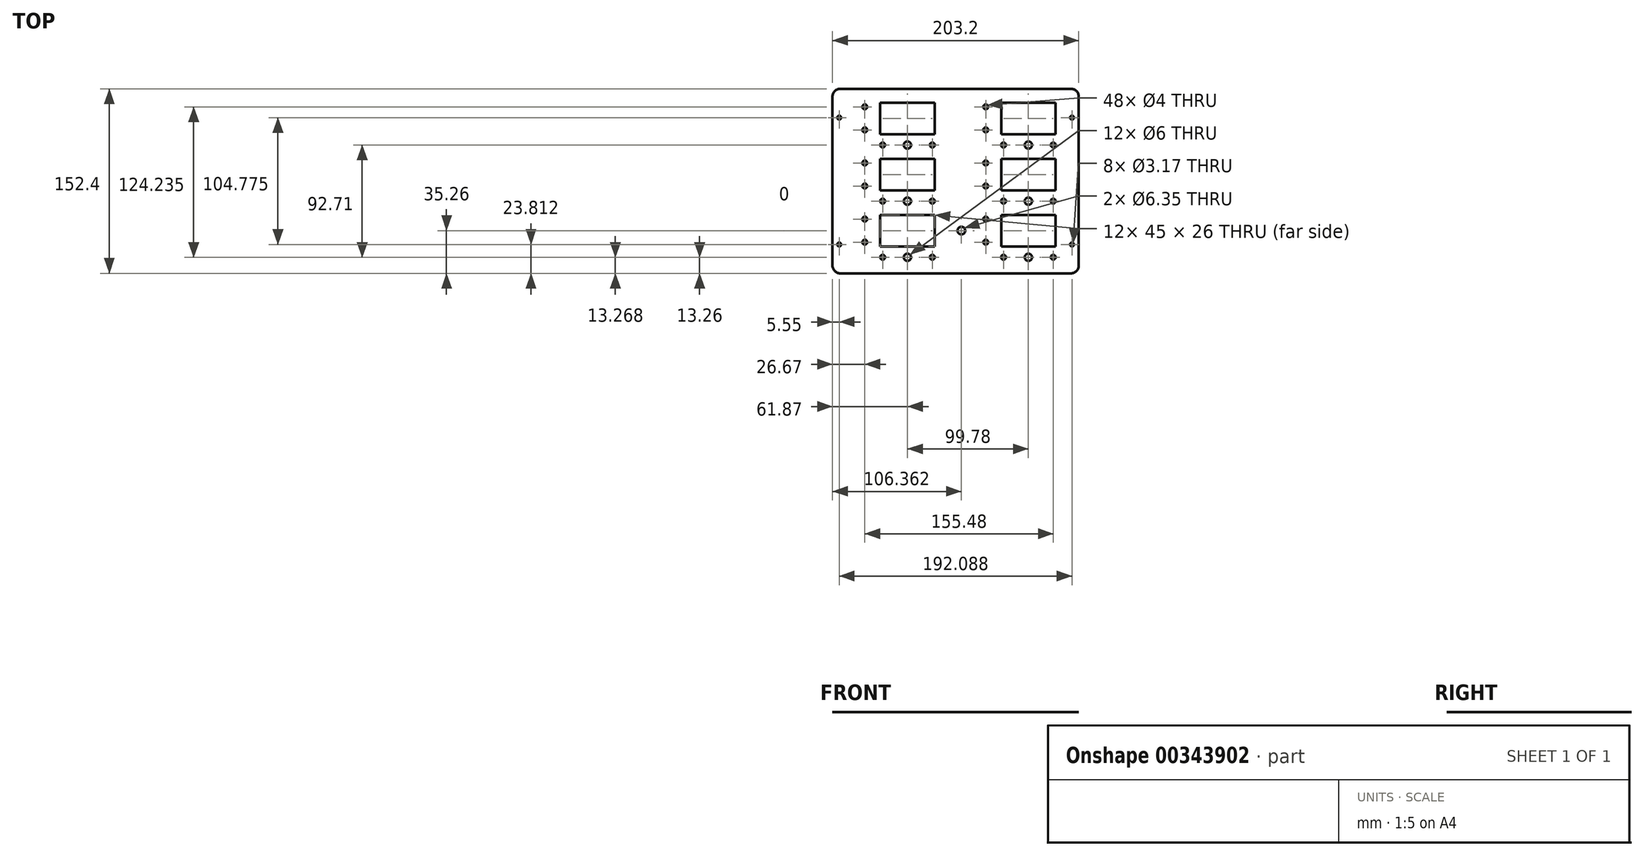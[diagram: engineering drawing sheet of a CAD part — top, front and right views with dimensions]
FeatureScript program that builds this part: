
annotation { "Feature Type Name" : "Feature", "Feature Type Description" : "" }
export const myFeature = defineFeature(function(context is Context, id is Id, definition is map)
    precondition{}
    {
        {
            var Q0;
            Q0=qCreatedBy(makeId("Top.planeOp"),FACE);
            var sketch = newSketch(context, id + "F0", { "sketchPlane" : qUnion([Q0])});
            skLineSegment(sketch, "E0.bottom", {"start": v(6.35, 0) * mm, "end": v(196.85, 0) * mm});
            skLineSegment(sketch, "E0.top", {"start": v(6.35, 152.4) * mm, "end": v(196.85, 152.4) * mm});
            skLineSegment(sketch, "E0.left", {"start": v(0, 6.35) * mm, "end": v(0, 146.05) * mm});
            skLineSegment(sketch, "E0.right", {"start": v(203.2, 6.35) * mm, "end": v(203.2, 146.05) * mm});
            skPoint(sketch, "E1.visualSharp", {"position": v(0, 0) * mm});
            skArc(sketch, "E1.filletArc", {"start": v(0, 6.35) * mm, "mid": v(1.86, 1.86) * mm, "end": v(6.35, 0) * mm});
            skPoint(sketch, "E2.visualSharp", {"position": v(203.2, 0) * mm});
            skArc(sketch, "E2.filletArc", {"start": v(196.85, 0) * mm, "mid": v(201.34, 1.86) * mm, "end": v(203.2, 6.35) * mm});
            skPoint(sketch, "E3.visualSharp", {"position": v(203.2, 152.4) * mm});
            skArc(sketch, "E3.filletArc", {"start": v(203.2, 146.05) * mm, "mid": v(201.34, 150.54) * mm, "end": v(196.85, 152.4) * mm});
            skPoint(sketch, "E4.visualSharp", {"position": v(0, 152.4) * mm});
            skArc(sketch, "E4.filletArc", {"start": v(6.35, 152.4) * mm, "mid": v(1.86, 150.54) * mm, "end": v(0, 146.05) * mm});
            skSolve(sketch);
        }
        {
            assignVariable(context, id + "F1", {"name" : "PanelTopLayer", "anyValue" : 1 / 1625.6 * mm});
        }
        {
            assignVariable(context, id + "F2", {"name" : "PanelDepth", "anyValue" : 3 / 812.8 * mm});
        }
        {
            var Q0;
            Q0=makeQuery(id+"F0.imprint","IMPRINT",FACE,{"disambiguationData":[TD([[makeQuery(id+"F0.imprint","IMPRINT",EDGE,{"derivedFrom":sQuery(id+"F0.wireOp",EDGE,"E0.bottom")}),1.0]])]});
            extrude(context, id + "F3", {"entities" : qUnion([Q0]), "oppositeDirection" : true, "depth" : getVariable(context, 'PanelTopLayer')});
        }
        {
            var Q0;
            Q0=makeQuery(id+"F3.opExtrude","CAP_FACE",FACE,{"disambiguationData":[OSD([sQuery(id+"F0.wireOp",EDGE,"E0.bottom"),sQuery(id+"F0.wireOp",EDGE,"E0.top"),sQuery(id+"F0.wireOp",EDGE,"E0.left"),sQuery(id+"F0.wireOp",EDGE,"E0.right"),sQuery(id+"F0.wireOp",EDGE,"4eb8843b-68a4-456e-adec-9ead3661f281.filletArc"),sQuery(id+"F0.wireOp",EDGE,"3b2eceeb-73e7-411c-82d1-259add97614e.filletArc"),sQuery(id+"F0.wireOp",EDGE,"241cabb4-3010-4474-995e-d7eb64fd05fc.filletArc"),sQuery(id+"F0.wireOp",EDGE,"ce37bbed-e9fa-4a66-9d02-96ea8e3f6179.filletArc")])],"isStart":false});
            var sketch = newSketch(context, id + "F4", { "sketchPlane" : qUnion([Q0])});
            skLineSegment(sketch, "E5.bottom", {"start": v(196.85, -152.4) * mm, "end": v(6.35, -152.4) * mm});
            skLineSegment(sketch, "E5.top", {"start": v(196.85, 0) * mm, "end": v(6.35, 0) * mm});
            skLineSegment(sketch, "E5.left", {"start": v(203.2, -146.05) * mm, "end": v(203.2, -6.35) * mm});
            skLineSegment(sketch, "E5.right", {"start": v(0, -146.05) * mm, "end": v(0, -6.35) * mm});
            skPoint(sketch, "E6.visualSharp", {"position": v(203.2, -152.4) * mm});
            skArc(sketch, "E6.filletArc", {"start": v(196.85, -152.4) * mm, "mid": v(201.34, -150.54) * mm, "end": v(203.2, -146.05) * mm});
            skPoint(sketch, "E7.visualSharp", {"position": v(0, -152.4) * mm});
            skArc(sketch, "E7.filletArc", {"start": v(0, -146.05) * mm, "mid": v(1.86, -150.54) * mm, "end": v(6.35, -152.4) * mm});
            skPoint(sketch, "E8.visualSharp", {"position": v(0, 0) * mm});
            skArc(sketch, "E8.filletArc", {"start": v(6.35, 0) * mm, "mid": v(1.86, -1.86) * mm, "end": v(0, -6.35) * mm});
            skPoint(sketch, "E9.visualSharp", {"position": v(203.2, 0) * mm});
            skArc(sketch, "E9.filletArc", {"start": v(203.2, -6.35) * mm, "mid": v(201.34, -1.86) * mm, "end": v(196.85, 0) * mm});
            skSolve(sketch);
        }
        {
            var Q0;
            Q0=makeQuery(id+"F4.imprint","IMPRINT",FACE,{"disambiguationData":[TD([[makeQuery(id+"F4.imprint","IMPRINT",EDGE,{"derivedFrom":sQuery(id+"F4.wireOp",EDGE,"E5.bottom")}),1.0]])]});
            extrude(context, id + "F5", {"entities" : qUnion([Q0]), "depth" : getVariable(context, 'PanelDepth') - getVariable(context, 'PanelTopLayer')});
        }
        {
            var Q0;
            Q0=makeQuery(id+"F0.imprint","IMPRINT",FACE,{"disambiguationData":[TD([[makeQuery(id+"F0.imprint","IMPRINT",EDGE,{"derivedFrom":sQuery(id+"F0.wireOp",EDGE,"E0.bottom")}),1.0]])]});
            var sketch = newSketch(context, id + "F6", { "sketchPlane" : qUnion([Q0])});
            skLineSegment(sketch, "E10.bottom", {"start": v(139.15, 140.97) * mm, "end": v(184.15, 140.97) * mm});
            skLineSegment(sketch, "E10.top", {"start": v(139.15, 114.97) * mm, "end": v(184.15, 114.97) * mm});
            skLineSegment(sketch, "E10.left", {"start": v(139.15, 140.97) * mm, "end": v(139.15, 114.97) * mm});
            skLineSegment(sketch, "E10.right", {"start": v(184.15, 140.97) * mm, "end": v(184.15, 114.97) * mm});
            skLineSegment(sketch, "E11.0.1.0", {"start": v(139.15, 94.62) * mm, "end": v(184.15, 94.62) * mm});
            skLineSegment(sketch, "E11.0.1.1", {"start": v(139.15, 94.62) * mm, "end": v(139.15, 68.62) * mm});
            skLineSegment(sketch, "E11.0.1.2", {"start": v(139.15, 68.62) * mm, "end": v(184.15, 68.62) * mm});
            skLineSegment(sketch, "E11.0.1.3", {"start": v(184.15, 94.62) * mm, "end": v(184.15, 68.62) * mm});
            skLineSegment(sketch, "E11.0.2.0", {"start": v(139.15, 48.26) * mm, "end": v(184.15, 48.26) * mm});
            skLineSegment(sketch, "E11.0.2.1", {"start": v(139.15, 48.26) * mm, "end": v(139.15, 22.26) * mm});
            skLineSegment(sketch, "E11.0.2.2", {"start": v(139.15, 22.26) * mm, "end": v(184.15, 22.26) * mm});
            skLineSegment(sketch, "E11.0.2.3", {"start": v(184.15, 48.26) * mm, "end": v(184.15, 22.26) * mm});
            skLineSegment(sketch, "E11.1.0.0", {"start": v(39.37, 140.97) * mm, "end": v(84.37, 140.97) * mm});
            skLineSegment(sketch, "E11.1.0.1", {"start": v(39.37, 140.97) * mm, "end": v(39.37, 114.97) * mm});
            skLineSegment(sketch, "E11.1.0.2", {"start": v(39.37, 114.97) * mm, "end": v(84.37, 114.97) * mm});
            skLineSegment(sketch, "E11.1.0.3", {"start": v(84.37, 140.97) * mm, "end": v(84.37, 114.97) * mm});
            skLineSegment(sketch, "E11.1.1.0", {"start": v(39.37, 94.62) * mm, "end": v(84.37, 94.62) * mm});
            skLineSegment(sketch, "E11.1.1.1", {"start": v(39.37, 94.62) * mm, "end": v(39.37, 68.62) * mm});
            skLineSegment(sketch, "E11.1.1.2", {"start": v(39.37, 68.62) * mm, "end": v(84.37, 68.62) * mm});
            skLineSegment(sketch, "E11.1.1.3", {"start": v(84.37, 94.62) * mm, "end": v(84.37, 68.62) * mm});
            skLineSegment(sketch, "E11.1.2.0", {"start": v(39.37, 48.26) * mm, "end": v(84.37, 48.26) * mm});
            skLineSegment(sketch, "E11.1.2.1", {"start": v(39.37, 48.26) * mm, "end": v(39.37, 22.26) * mm});
            skLineSegment(sketch, "E11.1.2.2", {"start": v(39.37, 22.26) * mm, "end": v(84.37, 22.26) * mm});
            skLineSegment(sketch, "E11.1.2.3", {"start": v(84.37, 48.26) * mm, "end": v(84.37, 22.26) * mm});
            skLineSegment(sketch, "E11.direction1", {"start": v(139.15, 114.97) * mm, "end": v(39.37, 114.97) * mm, "construction": true});
            skLineSegment(sketch, "E11.direction2", {"start": v(139.15, 114.97) * mm, "end": v(139.15, 68.62) * mm, "construction": true});
            skSolve(sketch);
        }
        {
            var Q0;
            Q0=qSketchRegion(id+"F6",true);
            extrude(context, id + "F7", {"entities" : qUnion([Q0]), "operationType" : NewBodyOperationType.REMOVE, "oppositeDirection" : true, "depth" : (getVariable(context, 'PanelDepth'))});
        }
        {
            var Q0;
            Q0=makeQuery(id+"F0.imprint","IMPRINT",FACE,{"disambiguationData":[TD([[makeQuery(id+"F0.imprint","IMPRINT",EDGE,{"derivedFrom":sQuery(id+"F0.wireOp",EDGE,"E0.bottom")}),1.0]])]});
            var sketch = newSketch(context, id + "F8", { "sketchPlane" : qUnion([Q0])});
            skCircle(sketch, "E12", {"center": v(106.36, 35.26) * mm, "radius": 3.18 * mm});
            skCircle(sketch, "E13", {"center": v(126.45, 137.5) * mm, "radius": 2 * mm});
            skLineSegment(sketch, "E14.direction1", {"start": v(105.19, 137.5) * mm, "end": v(126.45, 137.5) * mm, "construction": true});
            skLineSegment(sketch, "E14.direction2", {"start": v(126.45, 137.5) * mm, "end": v(126.45, 118.44) * mm, "construction": true});
            skCircle(sketch, "E15", {"center": v(141.15, 105.97) * mm, "radius": 2 * mm});
            skCircle(sketch, "E16.1.0.0", {"center": v(182.15, 105.97) * mm, "radius": 2 * mm});
            skLineSegment(sketch, "E16.direction1", {"start": v(141.15, 105.97) * mm, "end": v(182.15, 105.97) * mm, "construction": true});
            skCircle(sketch, "E17.0.0.1", {"center": v(126.45, 118.44) * mm, "radius": 2 * mm});
            skCircle(sketch, "E18.0.1.0", {"center": v(182.15, 59.62) * mm, "radius": 2 * mm});
            skCircle(sketch, "E18.0.1.1", {"center": v(141.15, 59.62) * mm, "radius": 2 * mm});
            skLineSegment(sketch, "E18.0.1.2", {"start": v(141.15, 59.62) * mm, "end": v(182.15, 59.62) * mm, "construction": true});
            skCircle(sketch, "E18.0.1.3", {"center": v(126.45, 91.14) * mm, "radius": 2 * mm});
            skCircle(sketch, "E18.0.1.4", {"center": v(126.45, 72.09) * mm, "radius": 2 * mm});
            skLineSegment(sketch, "E18.0.1.5", {"start": v(126.45, 91.14) * mm, "end": v(126.45, 72.1) * mm, "construction": true});
            skLineSegment(sketch, "E18.0.1.6", {"start": v(105.19, 91.14) * mm, "end": v(126.45, 91.14) * mm, "construction": true});
            skCircle(sketch, "E18.0.2.0", {"center": v(182.15, 13.26) * mm, "radius": 2 * mm});
            skCircle(sketch, "E18.0.2.1", {"center": v(141.15, 13.26) * mm, "radius": 2 * mm});
            skLineSegment(sketch, "E18.0.2.2", {"start": v(141.15, 13.26) * mm, "end": v(182.15, 13.26) * mm, "construction": true});
            skCircle(sketch, "E18.0.2.3", {"center": v(126.45, 44.79) * mm, "radius": 2 * mm});
            skCircle(sketch, "E18.0.2.4", {"center": v(126.45, 25.73) * mm, "radius": 2 * mm});
            skLineSegment(sketch, "E18.0.2.5", {"start": v(126.45, 44.79) * mm, "end": v(126.45, 25.73) * mm, "construction": true});
            skLineSegment(sketch, "E18.0.2.6", {"start": v(105.19, 44.79) * mm, "end": v(126.45, 44.79) * mm, "construction": true});
            skCircle(sketch, "E18.1.0.0", {"center": v(82.37, 105.97) * mm, "radius": 2 * mm});
            skCircle(sketch, "E18.1.0.1", {"center": v(41.37, 105.97) * mm, "radius": 2 * mm});
            skLineSegment(sketch, "E18.1.0.2", {"start": v(41.37, 105.97) * mm, "end": v(82.37, 105.97) * mm, "construction": true});
            skCircle(sketch, "E18.1.0.3", {"center": v(26.67, 137.5) * mm, "radius": 2 * mm});
            skCircle(sketch, "E18.1.0.4", {"center": v(26.67, 118.44) * mm, "radius": 2 * mm});
            skLineSegment(sketch, "E18.1.0.5", {"start": v(26.67, 137.5) * mm, "end": v(26.67, 118.44) * mm, "construction": true});
            skLineSegment(sketch, "E18.1.0.6", {"start": v(5.4, 137.5) * mm, "end": v(26.67, 137.5) * mm, "construction": true});
            skCircle(sketch, "E18.1.1.0", {"center": v(82.37, 59.62) * mm, "radius": 2 * mm});
            skCircle(sketch, "E18.1.1.1", {"center": v(41.37, 59.62) * mm, "radius": 2 * mm});
            skLineSegment(sketch, "E18.1.1.2", {"start": v(41.37, 59.62) * mm, "end": v(82.37, 59.62) * mm, "construction": true});
            skCircle(sketch, "E18.1.1.3", {"center": v(26.67, 91.14) * mm, "radius": 2 * mm});
            skCircle(sketch, "E18.1.1.4", {"center": v(26.67, 72.09) * mm, "radius": 2 * mm});
            skLineSegment(sketch, "E18.1.1.5", {"start": v(26.67, 91.14) * mm, "end": v(26.67, 72.09) * mm, "construction": true});
            skLineSegment(sketch, "E18.1.1.6", {"start": v(5.4, 91.14) * mm, "end": v(26.67, 91.14) * mm, "construction": true});
            skCircle(sketch, "E18.1.2.0", {"center": v(82.37, 13.26) * mm, "radius": 2 * mm});
            skCircle(sketch, "E18.1.2.1", {"center": v(41.37, 13.26) * mm, "radius": 2 * mm});
            skLineSegment(sketch, "E18.1.2.2", {"start": v(41.37, 13.26) * mm, "end": v(82.37, 13.26) * mm, "construction": true});
            skCircle(sketch, "E18.1.2.3", {"center": v(26.67, 44.79) * mm, "radius": 2 * mm});
            skCircle(sketch, "E18.1.2.4", {"center": v(26.67, 25.73) * mm, "radius": 2 * mm});
            skLineSegment(sketch, "E18.1.2.5", {"start": v(26.67, 44.79) * mm, "end": v(26.67, 25.73) * mm, "construction": true});
            skLineSegment(sketch, "E18.1.2.6", {"start": v(5.4, 44.79) * mm, "end": v(26.67, 44.79) * mm, "construction": true});
            skLineSegment(sketch, "E18.direction1", {"start": v(126.45, 118.44) * mm, "end": v(26.67, 118.44) * mm, "construction": true});
            skLineSegment(sketch, "E18.direction2", {"start": v(126.45, 118.44) * mm, "end": v(126.45, 72.1) * mm, "construction": true});
            skSolve(sketch);
        }
        {
            var Q0;
            Q0=makeQuery(id+"F0.imprint","IMPRINT",FACE,{"disambiguationData":[TD([[makeQuery(id+"F0.imprint","IMPRINT",EDGE,{"derivedFrom":sQuery(id+"F0.wireOp",EDGE,"E0.bottom")}),1.0]])]});
            var sketch = newSketch(context, id + "F9", { "sketchPlane" : qUnion([Q0])});
            skCircle(sketch, "E19", {"center": v(161.65, 105.98) * mm, "radius": 3 * mm});
            skCircle(sketch, "E20.0.1.0", {"center": v(161.65, 59.62) * mm, "radius": 3 * mm});
            skCircle(sketch, "E20.0.2.0", {"center": v(161.65, 13.27) * mm, "radius": 3 * mm});
            skCircle(sketch, "E20.1.0.0", {"center": v(61.87, 105.98) * mm, "radius": 3 * mm});
            skCircle(sketch, "E20.1.1.0", {"center": v(61.87, 59.62) * mm, "radius": 3 * mm});
            skCircle(sketch, "E20.1.2.0", {"center": v(61.87, 13.27) * mm, "radius": 3 * mm});
            skLineSegment(sketch, "E20.direction1", {"start": v(161.65, 105.98) * mm, "end": v(61.87, 105.98) * mm, "construction": true});
            skLineSegment(sketch, "E20.direction2", {"start": v(161.65, 105.98) * mm, "end": v(161.65, 59.62) * mm, "construction": true});
            skSolve(sketch);
        }
        {
            var Q0;
            Q0=qSketchRegion(id+"F8",true);
            extrude(context, id + "F10", {"entities" : qUnion([Q0]), "operationType" : NewBodyOperationType.REMOVE, "oppositeDirection" : true, "depth" : (getVariable(context, 'PanelDepth'))});
        }
        {
            var Q0;
            Q0=qSketchRegion(id+"F9",true);
            extrude(context, id + "F11", {"entities" : qUnion([Q0]), "operationType" : NewBodyOperationType.REMOVE, "oppositeDirection" : true, "depth" : (getVariable(context, 'PanelDepth'))});
        }
        {
            var Q0;
            Q0=makeQuery(id+"F0.imprint","IMPRINT",FACE,{"disambiguationData":[TD([[makeQuery(id+"F0.imprint","IMPRINT",EDGE,{"derivedFrom":sQuery(id+"F0.wireOp",EDGE,"E0.bottom")}),1.0]])]});
            var sketch = newSketch(context, id + "F12", { "sketchPlane" : qUnion([Q0])});
            skCircle(sketch, "E21", {"center": v(5.55, 128.59) * mm, "radius": 1.59 * mm});
            skCircle(sketch, "E22.0.1.0", {"center": v(5.55, 23.81) * mm, "radius": 1.59 * mm});
            skCircle(sketch, "E22.1.0.0", {"center": v(197.64, 128.59) * mm, "radius": 1.59 * mm});
            skCircle(sketch, "E22.1.1.0", {"center": v(197.64, 23.81) * mm, "radius": 1.59 * mm});
            skLineSegment(sketch, "E22.direction1", {"start": v(5.55, 128.59) * mm, "end": v(197.64, 128.59) * mm, "construction": true});
            skLineSegment(sketch, "E22.direction2", {"start": v(5.55, 128.59) * mm, "end": v(5.55, 23.81) * mm, "construction": true});
            skSolve(sketch);
        }
        {
            var Q0;
            Q0 = qSketchRegion(id + "F12", true);
            extrude(context, id + "F13", {"entities" : qUnion([Q0]), "operationType" : NewBodyOperationType.REMOVE, "oppositeDirection" : true, "depth" : getVariable(context, 'PanelDepth')});
        }
    });
